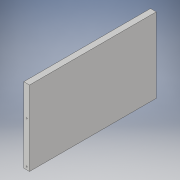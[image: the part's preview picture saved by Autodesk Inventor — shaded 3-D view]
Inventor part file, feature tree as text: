
AUTODESK INVENTOR PART (.ipt)
format: ipt  version: 2018 (Build 220112000, 112)  size: 103,424 bytes
history: native  units: in
note: dims shown in document units (in); Inventor stores cm internally (conversion verified against a paired STEP export)
features: sketch x2, extrude x2
ambient origin geometry x8: Origin, YZ Plane, XZ Plane, XY Plane, X Axis, Y Axis, Z Axis, Center Point
bodies: Body1 (feature_tree)
feature tree (4):
  sketch  "Sketch2"  dims[d0=13.0in d1=22.0in]
  extrude  "Extrusion2"  Depth=22.0in
  extrude  "Extrusion4"  Depth=1.0in TaperAngle=0.0deg
  sketch  "Sketch4"  dims[d6=1.0in d7=0.0in d15=36.0in d16=0.0in d25=0.5in d26=0.2031in d27=7.237in d28=0.2031in]
